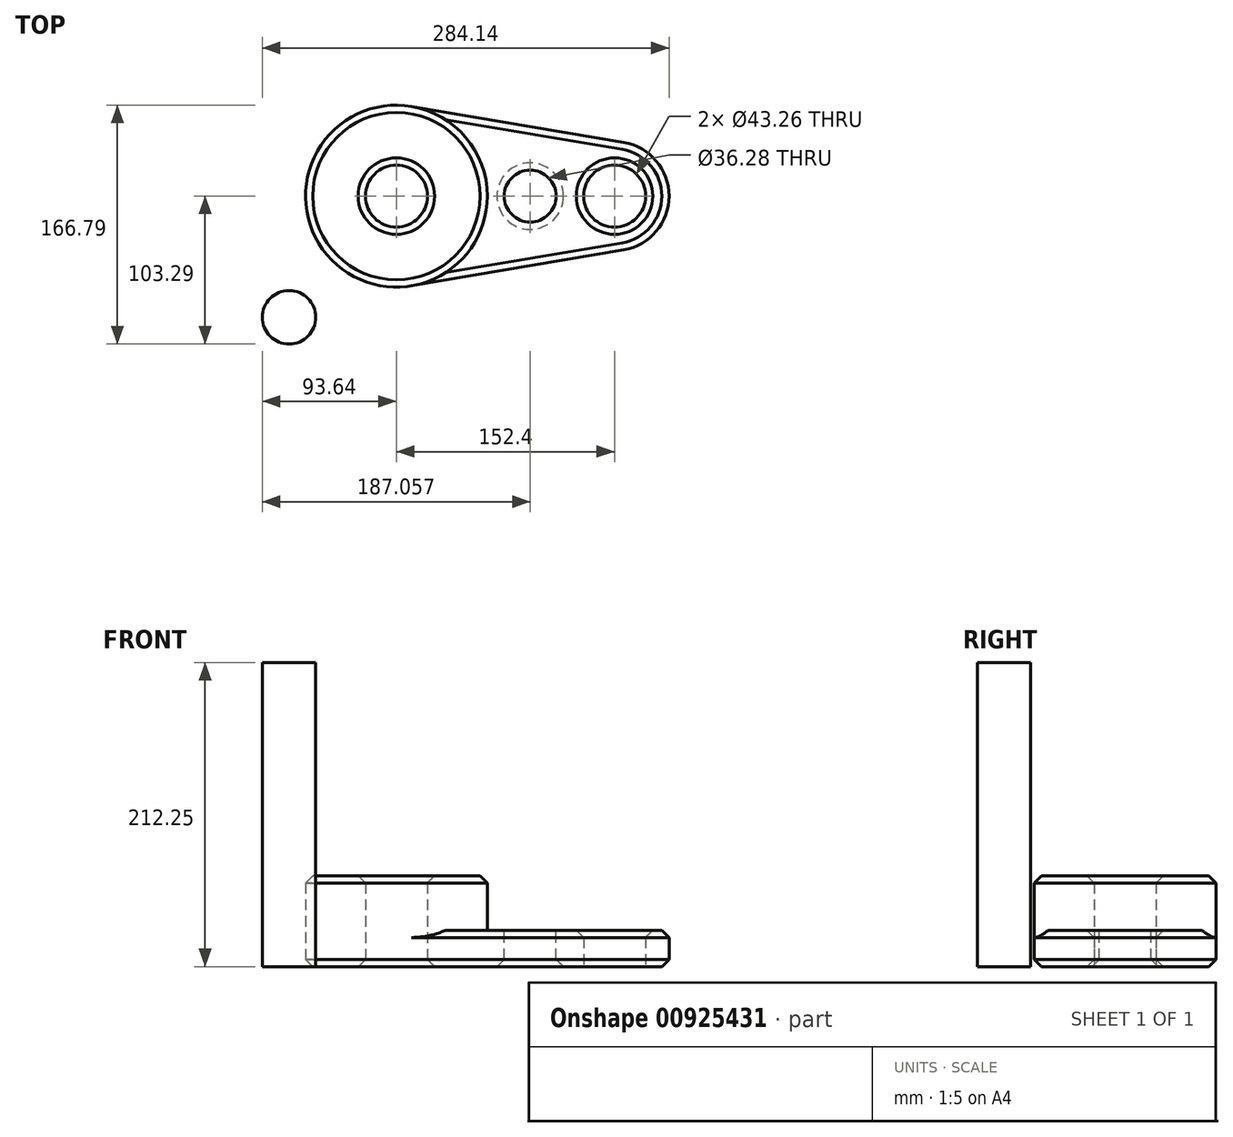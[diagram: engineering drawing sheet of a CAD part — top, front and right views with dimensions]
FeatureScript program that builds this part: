
annotation { "Feature Type Name" : "Feature", "Feature Type Description" : "" }
export const myFeature = defineFeature(function(context is Context, id is Id, definition is map)
    precondition{}
    {
        {
            var Q0;
            Q0=qCreatedBy(makeId("Top.planeOp"),FACE);
            var sketch = newSketch(context, id + "F0", { "sketchPlane" : qUnion([Q0])});
            skCircle(sketch, "E0", {"center": v(0, 0) * mm, "radius": 63.5 * mm});
            skCircle(sketch, "E1", {"center": v(152.4, 0) * mm, "radius": 38.1 * mm});
            skLineSegment(sketch, "E2", {"start": v(10.58, 62.61) * mm, "end": v(158.75, 37.57) * mm});
            skLineSegment(sketch, "E3", {"start": v(10.58, -62.61) * mm, "end": v(158.75, -37.57) * mm});
            skCircle(sketch, "E4", {"center": v(0, 0) * mm, "radius": 21.63 * mm});
            skCircle(sketch, "E5", {"center": v(152.4, 0) * mm, "radius": 21.63 * mm});
            skSolve(sketch);
        }
        {
            var Q0;
            Q0=makeQuery(id+"F0.imprint","IMPRINT",FACE,{"disambiguationData":[TD([[makeQuery(id+"F0.imprint","IMPRINT",EDGE,{"derivedFrom":sQuery(id+"F0.wireOp",EDGE,"E5")}),-1.0]])]});
            var Q1;
            {var subQ0=sQuery(id+"F0.wireOp",EDGE,"E2");Q1=makeQuery(id+"F0.imprint","IMPRINT",FACE,{"disambiguationData":[TD([[makeQuery(id+"F0.imprint","IMPRINT",EDGE,{"derivedFrom":subQ0}),-1.0]])]});}
            var Q2;
            Q2=makeQuery(id+"F0.imprint","IMPRINT",FACE,{"disambiguationData":[TD([[makeQuery(id+"F0.imprint","IMPRINT",EDGE,{"derivedFrom":sQuery(id+"F0.wireOp",EDGE,"E4")}),-1.0]])]});
            extrude(context, id + "F1", {"entities" : qUnion([Q0, Q1, Q2]), "depth" : 25.4 * mm, "offsetDistance" : 25.4 * mm});
        }
        {
            var Q0;
            Q0=makeQuery(id+"F0.imprint","IMPRINT",FACE,{"disambiguationData":[TD([[makeQuery(id+"F0.imprint","IMPRINT",EDGE,{"derivedFrom":sQuery(id+"F0.wireOp",EDGE,"E4")}),-1.0]])]});
            extrude(context, id + "F2", {"entities" : qUnion([Q0]), "operationType" : NewBodyOperationType.ADD, "depth" : 63.5 * mm, "offsetDistance" : 25.4 * mm});
        }
        {
            var Q0;
            Q0=makeQuery(id+"F2.opExtrude","CAP_EDGE",EDGE,{"disambiguationData":[OSD([sQuery(id+"F0.wireOp",EDGE,"E4")])],"isStart":false});
            var Q1;
            Q1=makeQuery(id+"F1.opExtrude","CAP_EDGE",EDGE,{"disambiguationData":[OSD([sQuery(id+"F0.wireOp",EDGE,"E5")])],"isStart":false});
            var Q2;
            Q2=makeQuery(id+"F1.opExtrude","CAP_EDGE",EDGE,{"disambiguationData":[OSD([sQuery(id+"F0.wireOp",EDGE,"E3")])],"isStart":false});
            var Q3;
            Q3=makeQuery(id+"F1.opExtrude","CAP_EDGE",EDGE,{"disambiguationData":[OSD([sQuery(id+"F0.wireOp",EDGE,"E1")])],"isStart":false});
            var Q4;
            Q4=makeQuery(id+"F1.opExtrude","CAP_EDGE",EDGE,{"disambiguationData":[OSD([sQuery(id+"F0.wireOp",EDGE,"E2")])],"isStart":false});
            var Q5;
            Q5=makeQuery(id+"F2.opExtrude","CAP_EDGE",EDGE,{"disambiguationData":[OSD([sQuery(id+"F0.wireOp",EDGE,"E0")])],"isStart":false});
            var Q6;
            Q6=makeQuery(id+"F1.opExtrude","CAP_EDGE",EDGE,{"disambiguationData":[OSD([sQuery(id+"F0.wireOp",EDGE,"E3")])],"isStart":true});
            var Q7;
            Q7=makeQuery(id+"F1.opExtrude","CAP_EDGE",EDGE,{"disambiguationData":[OSD([sQuery(id+"F0.wireOp",EDGE,"E4")])],"isStart":true});
            chamfer(context, id + "F3", {"entities" : qUnion([Q0, Q1, Q2, Q3, Q4, Q5, Q6, Q7]), "width" : 5.08 * mm, "tangentPropagation" : true});
        }
        {
            var Q0;
            Q0=makeQuery(id+"F1.opExtrude","CAP_FACE",FACE,{"disambiguationData":[OSD([sQuery(id+"F0.wireOp",EDGE,"E0"),sQuery(id+"F0.wireOp",EDGE,"E1"),sQuery(id+"F0.wireOp",EDGE,"E2"),sQuery(id+"F0.wireOp",EDGE,"E3"),sQuery(id+"F0.wireOp",EDGE,"E4"),sQuery(id+"F0.wireOp",EDGE,"E5")])],"isStart":false});
            var sketch = newSketch(context, id + "F4", { "sketchPlane" : qUnion([Q0])});
            skCircle(sketch, "E6", {"center": v(93.42, 0) * mm, "radius": 18.14 * mm});
            skSolve(sketch);
        }
        {
            var Q0;
            Q0 = qSketchRegion(id + "F4", true);
            extrude(context, id + "F5", {"entities" : qUnion([Q0]), "operationType" : NewBodyOperationType.REMOVE, "oppositeDirection" : true, "depth" : 69.01 * mm, "offsetDistance" : 25.4 * mm});
        }
        {
            var Q0;
            Q0=makeQuery(id+"F5.boolean.opBoolean","COPY",EDGE,{"derivedFrom":makeQuery(id+"F5.opExtrude","CAP_EDGE",EDGE,{"disambiguationData":[OSD([sQuery(id+"F4.wireOp",EDGE,"E6")])],"isStart":true})});
            var Q1;
            Q1=makeQuery(id+"F5.boolean.opBoolean","INTERSECT",EDGE,{"derivedFrom":[makeQuery(id+"F1.opExtrude","CAP_FACE",FACE,{"disambiguationData":[OSD([sQuery(id+"F0.wireOp",EDGE,"E0"),sQuery(id+"F0.wireOp",EDGE,"E1"),sQuery(id+"F0.wireOp",EDGE,"E2"),sQuery(id+"F0.wireOp",EDGE,"E3"),sQuery(id+"F0.wireOp",EDGE,"E4"),sQuery(id+"F0.wireOp",EDGE,"E5")])],"isStart":true}),makeQuery(id+"F5.opExtrude","SWEPT_FACE",FACE,{"disambiguationData":[OSD([sQuery(id+"F4.wireOp",EDGE,"E6")])]})]});
            chamfer(context, id + "F6", {"entities" : qUnion([Q0, Q1]), "width" : 5.08 * mm, "tangentPropagation" : true});
        }
        {
            var Q0;
            Q0=qCreatedBy(makeId("Top.planeOp"),FACE);
            var sketch = newSketch(context, id + "F7", { "sketchPlane" : qUnion([Q0])});
            skCircle(sketch, "E7", {"center": v(-74.96, -84.6) * mm, "radius": 18.68 * mm});
            skSolve(sketch);
        }
        {
            var Q0;
            Q0 = qSketchRegion(id + "F7", true);
            extrude(context, id + "F8", {"entities" : qUnion([Q0]), "depth" : 212.25 * mm, "offsetDistance" : 25.4 * mm});
        }
    });
